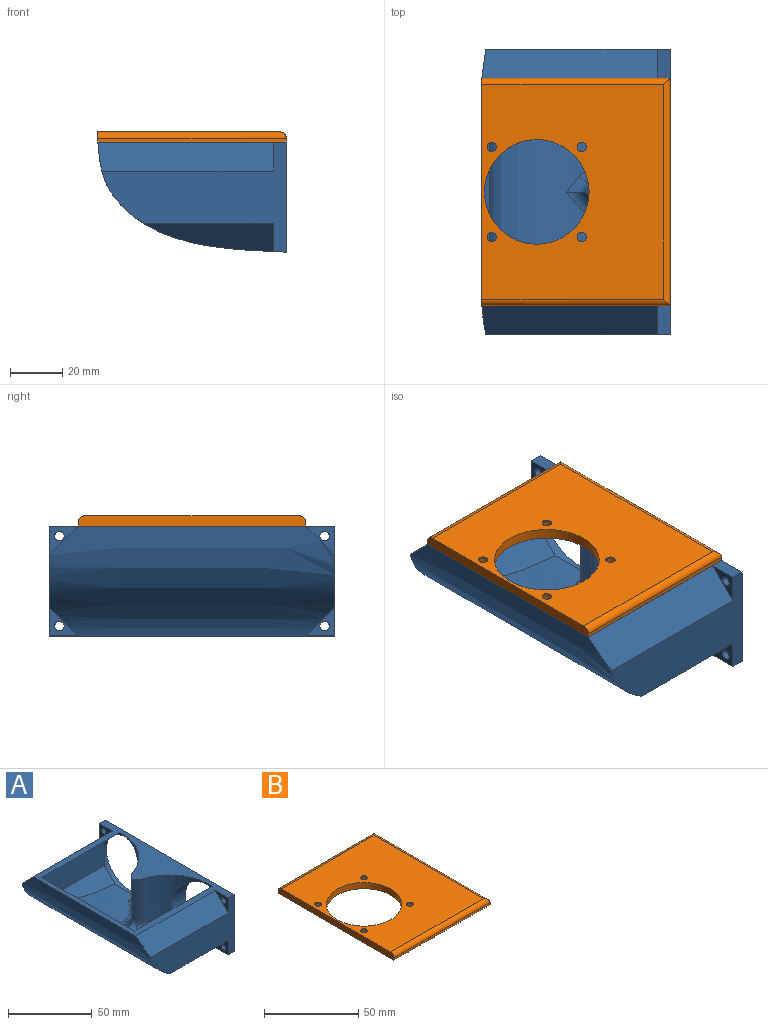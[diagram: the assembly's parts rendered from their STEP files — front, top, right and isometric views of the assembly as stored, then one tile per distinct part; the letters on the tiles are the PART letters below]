
ASSEMBLY  parts=2 mates=1
PART A: 58 faces, bbox 78x115x48 mm
  f0: plane 5.27x3.04mm, normal (-1,0,0), area 6.1mm2, adj f9,f23,f32,f34
  f1: extruded ~103x64.99mm, area 7057.8mm2, adj f9,f19,f20,f22,f23,f24,f25,f26
  f2: plane 5.27x3.04mm, normal (-1,0,0), area 6.1mm2, adj f9,f22,f26,f35
  f3: plane 0.08x0.04mm, normal (-1,0,0), area 0mm2, adj f19,f22,f26
  f4: plane 0.08x0.04mm, normal (-1,0,0), area 0mm2, adj f20,f24,f32
  f5: plane 0.08x0.04mm, normal (-1,0,0), area 0mm2, adj f20,f23,f32
  f6: extruded ~109x72mm, area 9319.6mm2, adj f7,f8,f9,f10,f11,f13,f15,f16
  f7: plane 70.74x42mm, normal (0,-1,0), area 1402.9mm2, adj f6,f9,f10,f11,f12,f17,f18
  f8: plane 70.74x42mm, normal (0,1,0), area 1402.9mm2, adj f6,f9,f10,f13,f14,f15,f16
  f9: plane 109x72mm, normal (0,0,1), area 1851.2mm2, adj f0,f1,f2,f6,f7,f8,f10,f11
  f10: plane 109x42mm, normal (1,0,0), area 1983.3mm2, adj f6,f7,f8,f9,f26,f32,f36,f37
  f11: plane 67.09x11.09mm, normal (0,-0.71,0.71), area 1032.8mm2, adj f6,f7,f9,f12
  f12: plane 11x11mm, normal (-1,0,0), area 50.3mm2, adj f7,f9,f11,f39
  f13: plane 67.09x11.09mm, normal (0,0.71,0.71), area 1032.8mm2, adj f6,f8,f9,f14
  f14: plane 11x11mm, normal (-1,0,0), area 50.3mm2, adj f8,f9,f13,f38
  f15: plane 49.5x10.78mm, normal (0,0.71,-0.71), area 530.2mm2, adj f6,f8,f16
  f16: plane 10.78x10.78mm, normal (-1,0,0), area 47.9mm2, adj f6,f8,f15,f37
  f17: plane 49.5x10.78mm, normal (0,-0.71,-0.71), area 530.2mm2, adj f6,f7,f18
  f18: plane 10.78x10.78mm, normal (-1,0,0), area 47.9mm2, adj f6,f7,f17,f36
  f19: plane 65.58x19.09mm, normal (0,1,0), area 996.5mm2, adj f1,f3,f21,f22,f25,f26,f27
  f20: plane 65.58x19.09mm, normal (0,-1,0), area 996.5mm2, adj f1,f4,f5,f23,f24,f30,f32
  f21: plane 0.08x0.04mm, normal (-1,0,0), area 0mm2, adj f19,f25,f26
  f22: plane 66.46x12.71mm, normal (0,0.71,-0.71), area 1116.6mm2, adj f1,f2,f3,f9,f19,f26,f28
  f23: plane 66.46x12.71mm, normal (0,-0.71,-0.71), area 1116.6mm2, adj f0,f1,f5,f9,f20,f31,f32
  f24: plane 53.57x14.99mm, normal (0,-0.71,0.71), area 418.3mm2, adj f1,f4,f20,f32,f33
  f25: plane 53.67x15.09mm, normal (0,0.71,0.71), area 418.3mm2, adj f1,f19,f21,f26,f29
  f26: cylinder r=20mm len=40mm, axis (1,0,0), area 753.2mm2, adj f1,f2,f3,f10,f19,f21,f22,f25
  f27: plane 17.44x2mm, normal (1,0,0), area 23.5mm2, adj f19,f26
  f28: plane 9.17x9.17mm, normal (1,0,0), area 9.4mm2, adj f22,f26
  f29: plane 27.04x11.21mm, normal (1,0,0), area 36mm2, adj f1,f25,f26
  f30: plane 17.44x2mm, normal (1,0,0), area 23.5mm2, adj f20,f32
  f31: plane 9.17x9.17mm, normal (1,0,0), area 9.4mm2, adj f23,f32
  f32: cylinder r=20mm len=40mm, axis (1,0,0), area 753.2mm2, adj f0,f1,f4,f5,f10,f20,f23,f24
  f33: plane 27.04x11.21mm, normal (1,0,0), area 36mm2, adj f1,f24,f32
  f34: cylinder r=34mm len=33.33mm, axis (0,0,-1), area 719.7mm2, adj f0,f9,f32,f53,f54
  f35: cylinder r=34mm len=33.33mm, axis (0,0,-1), area 719.6mm2, adj f2,f9,f26,f50,f51
  f36: cylinder r=1.8mm len=5mm, axis (1,0,0), area 56.5mm2, adj f10,f18
  f37: cylinder r=1.8mm len=5mm, axis (1,0,0), area 56.5mm2, adj f10,f16
  f38: cylinder r=1.8mm len=5mm, axis (1,0,0), area 56.5mm2, adj f10,f14
  f39: cylinder r=1.8mm len=5mm, axis (1,0,0), area 56.5mm2, adj f10,f12
  f40: cone r=0mm half-angle=59deg, axis (1,0,0), area 11.9mm2, adj f41
  f41: cylinder r=1.8mm len=5mm, axis (1,0,0), area 56.5mm2, adj f10,f40
  f42: cone r=0mm half-angle=59deg, axis (1,0,0), area 11.9mm2, adj f43
  f43: cylinder r=1.8mm len=5mm, axis (1,0,0), area 56.5mm2, adj f10,f42
  f44: cone r=0mm half-angle=59deg, axis (1,0,0), area 11.9mm2, adj f45
  f45: cylinder r=1.8mm len=5mm, axis (1,0,0), area 56.5mm2, adj f10,f44
  f46: cone r=0mm half-angle=59deg, axis (1,0,0), area 11.9mm2, adj f47
  f47: cylinder r=1.8mm len=5mm, axis (1,0,0), area 56.5mm2, adj f10,f46
  f48: plane 30.7x2.74mm, normal (-0.79,0.62,0), area 105.6mm2, adj f9,f49,f54,f57
  f49: plane 30.7x2.74mm, normal (-0.79,-0.62,0), area 105.6mm2, adj f9,f48,f50,f55
  f50: cylinder r=5mm len=31.68mm, axis (0,0,-1), area 96.2mm2, adj f9,f35,f49,f52
  f51: bspline ~25.01x22.49mm, area 196.4mm2, adj f1,f26,f35,f52
  f52: bspline ~9.12x7.84mm, area 36.9mm2, adj f1,f50,f51,f55
  f53: bspline ~24.68x21.6mm, area 196.3mm2, adj f1,f32,f34,f56
  f54: cylinder r=5mm len=31.68mm, axis (0,0,-1), area 96.2mm2, adj f9,f34,f48,f56
  f55: bspline ~14.77x13.84mm, area 49.5mm2, adj f1,f49,f52,f57
  f56: bspline ~9.11x8.17mm, area 36.9mm2, adj f1,f53,f54,f57
  f57: bspline ~14.77x13.84mm, area 49.5mm2, adj f1,f48,f55,f56
PART B: 22 faces, bbox 72x87x4 mm
  f0: plane 87x4mm, normal (-1,0,0), area 345.3mm2, adj f1,f3,f5,f6,f19,f21
  f1: plane 72x1.5mm, normal (0,-1,0), area 108mm2, adj f0,f2,f6,f19
  f2: plane 87x1.5mm, normal (1,0,0), area 130.5mm2, adj f1,f3,f6,f20
  f3: plane 72x1.5mm, normal (0,1,0), area 108mm2, adj f0,f2,f6,f21
  f4: cylinder r=20mm len=40mm, axis (0,0,-1), area 502.7mm2, adj f5,f6
  f5: plane 82x69.5mm, normal (0,0,1), area 4401.6mm2, adj f0,f4,f7,f10,f13,f16,f19,f20
  f6: plane 87x72mm, normal (0,0,-1), area 4874.6mm2, adj f0,f1,f2,f3,f4,f9,f12,f15
  f7: cylinder r=1.8mm len=3.6mm, axis (0,0,-1), area 6.8mm2, adj f5,f8
  f8: plane 6.5x6.5mm, normal (0,0,-1), area 23mm2, adj f7,f9
  f9: cylinder r=3.25mm len=6.5mm, axis (0,0,-1), area 69.4mm2, adj f6,f8
  f10: cylinder r=1.8mm len=3.6mm, axis (0,0,-1), area 6.8mm2, adj f5,f11
  f11: plane 6.5x6.5mm, normal (0,0,-1), area 23mm2, adj f10,f12
  f12: cylinder r=3.25mm len=6.5mm, axis (0,0,-1), area 69.4mm2, adj f6,f11
  f13: cylinder r=1.8mm len=3.6mm, axis (0,0,-1), area 6.8mm2, adj f5,f14
  f14: plane 6.5x6.5mm, normal (0,0,-1), area 23mm2, adj f13,f15
  f15: cylinder r=3.25mm len=6.5mm, axis (0,0,-1), area 69.4mm2, adj f6,f14
  f16: cylinder r=1.8mm len=3.6mm, axis (0,0,-1), area 6.8mm2, adj f5,f17
  f17: plane 6.5x6.5mm, normal (0,0,-1), area 23mm2, adj f16,f18
  f18: cylinder r=3.25mm len=6.5mm, axis (0,0,-1), area 69.4mm2, adj f6,f17
  f19: cylinder r=2.5mm len=72mm, axis (-1,0,0), area 279.2mm2, adj f0,f1,f5,f20
  f20: cylinder r=2.5mm len=87mm, axis (0,-1,0), area 334.5mm2, adj f2,f5,f19,f21
  f21: cylinder r=2.5mm len=72mm, axis (1,0,0), area 279.2mm2, adj f0,f3,f5,f20
PLACE A t=(-50.62,-64.32,-79.41)mm
PLACE B t=(-50.05,-249.02,-68.1)mm
MATE fastened A.f9 <-> B.f6  axis (0,0,1) through (-71.65,-107.82,-68.1)mm
